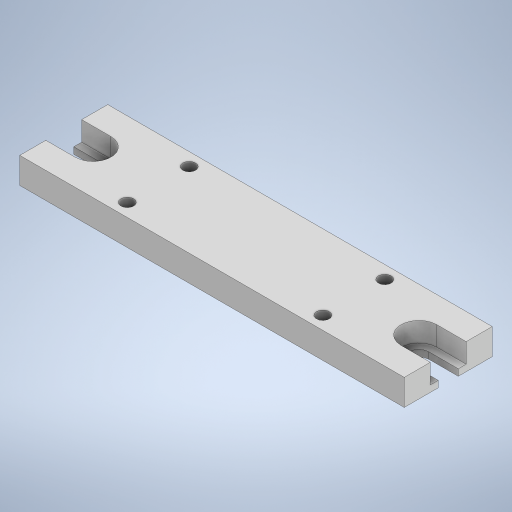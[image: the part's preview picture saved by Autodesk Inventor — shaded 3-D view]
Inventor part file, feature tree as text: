
AUTODESK INVENTOR PART (.ipt)
format: ipt  version: 2023 (Build 270158000, 158)  size: 457,216 bytes
history: native  units: mm
features: extrude x3, sketch x1
ambient origin geometry x8: Origin, YZ Plane, XZ Plane, XY Plane, X Axis, Y Axis, Z Axis, Center Point
bodies: Body1 (feature_tree)
feature tree (4):
  sketch  "Sketch1"  dims[d162=60.0mm d163=60.0mm d165=100.0mm d173=90.0mm d183=11.0mm d184=11.0mm d185=6.15mm d186=6.15mm d187=3.95mm d188=3.95mm d189=3.95mm d190=3.95mm d202=9.0mm d203=9.0mm d204=9.0mm d212=19.0mm d213=19.0mm d214=27.0mm d215=4.0mm d216=4.0mm d217=13.5mm d218=30.0mm d219=30.0mm d220=8.0mm d221=0.0mm d222=2.0mm d223=0.0mm d224=2.0mm d225=0.0mm]
  extrude  "Extrusion13"  Depth=11.0mm
  extrude  "Extrusion14"  Depth=11.0mm
  extrude  "Extrusion15"  Depth=6.15mm
